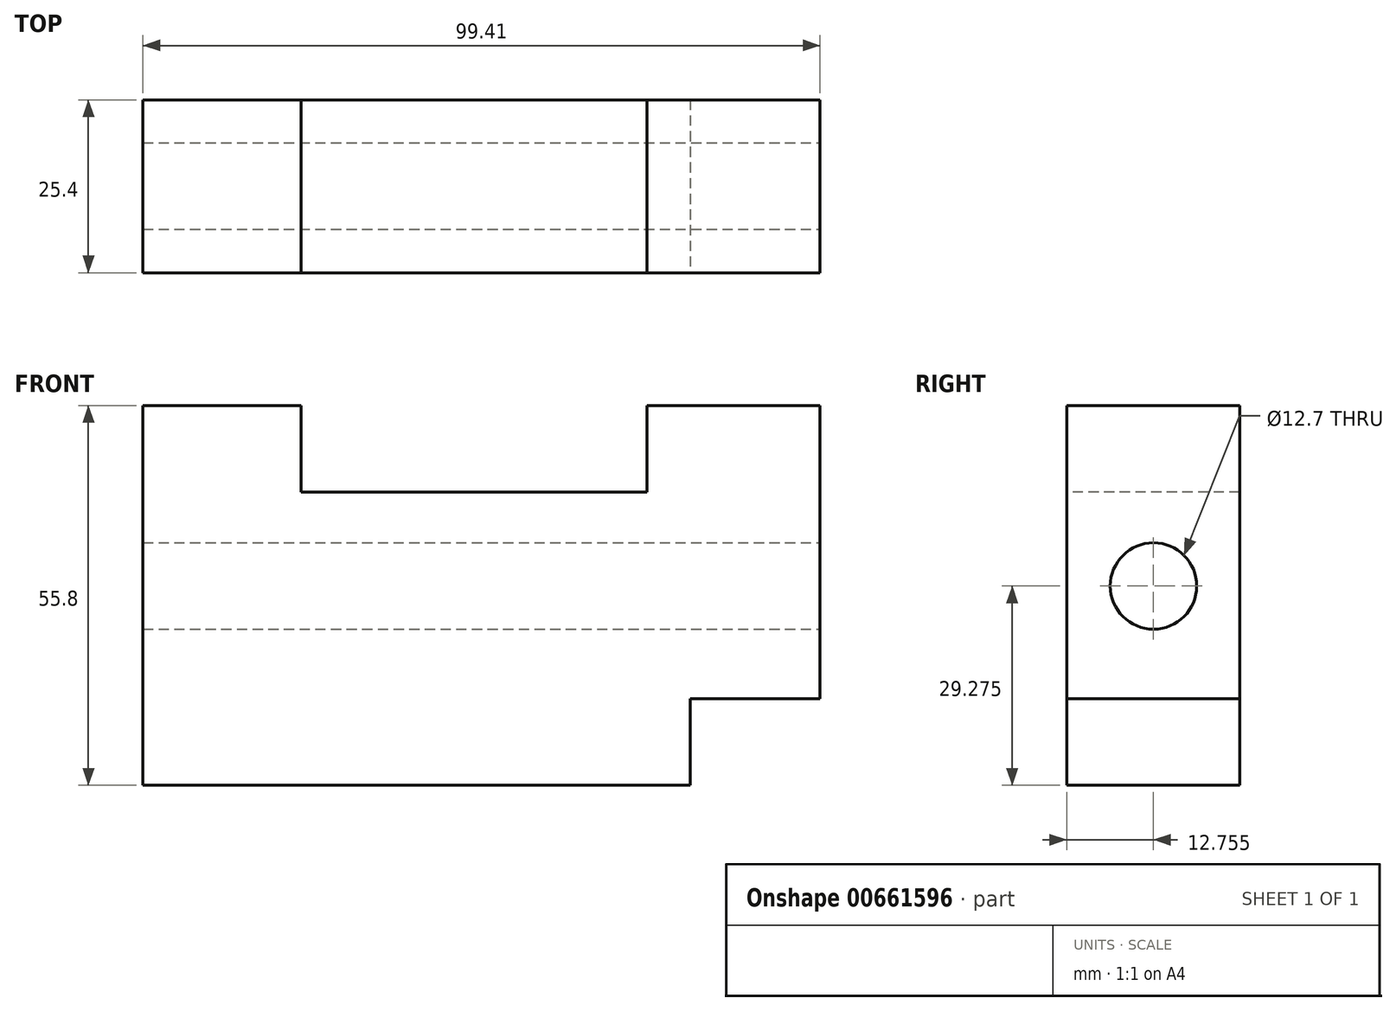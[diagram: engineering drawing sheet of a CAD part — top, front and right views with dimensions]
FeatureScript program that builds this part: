
annotation { "Feature Type Name" : "Feature", "Feature Type Description" : "" }
export const myFeature = defineFeature(function(context is Context, id is Id, definition is map)
    precondition{}
    {
        {
            var Q0;
            Q0=qCreatedBy(makeId("Front.planeOp"),FACE);
            var sketch = newSketch(context, id + "F0", { "sketchPlane" : qUnion([Q0])});
            skLineSegment(sketch, "E0.bottom", {"start": v(0, 0) * mm, "end": v(-99.41, 0) * mm});
            skLineSegment(sketch, "E0.top", {"start": v(0, 55.8) * mm, "end": v(-99.41, 55.8) * mm});
            skLineSegment(sketch, "E0.left", {"start": v(0, 0) * mm, "end": v(0, 55.8) * mm});
            skLineSegment(sketch, "E0.right", {"start": v(-99.41, 0) * mm, "end": v(-99.41, 55.8) * mm});
            skSolve(sketch);
        }
        {
            var Q0;
            Q0=makeQuery(id+"F0.imprint","IMPRINT",FACE,{"disambiguationData":[TD([[makeQuery(id+"F0.imprint","IMPRINT",EDGE,{"derivedFrom":sQuery(id+"F0.wireOp",EDGE,"E0.bottom")}),-1.0]])]});
            extrude(context, id + "F1", {"entities" : qUnion([Q0]), "depth" : 25.4 * mm, "offsetDistance" : 25.4 * mm});
        }
        {
            var Q0;
            Q0=makeQuery(id+"F1.opExtrude","CAP_FACE",FACE,{"disambiguationData":[OSD([sQuery(id+"F0.wireOp",EDGE,"E0.bottom"),sQuery(id+"F0.wireOp",EDGE,"E0.top"),sQuery(id+"F0.wireOp",EDGE,"E0.left"),sQuery(id+"F0.wireOp",EDGE,"E0.right")])],"isStart":false});
            var sketch = newSketch(context, id + "F2", { "sketchPlane" : qUnion([Q0])});
            skLineSegment(sketch, "E1.bottom", {"start": v(-76.2, 55.8) * mm, "end": v(-25.4, 55.8) * mm});
            skLineSegment(sketch, "E1.top", {"start": v(-76.2, 43.1) * mm, "end": v(-25.4, 43.1) * mm});
            skLineSegment(sketch, "E1.left", {"start": v(-76.2, 55.8) * mm, "end": v(-76.2, 43.1) * mm});
            skLineSegment(sketch, "E1.right", {"start": v(-25.4, 55.8) * mm, "end": v(-25.4, 43.1) * mm});
            skSolve(sketch);
        }
        {
            var Q0;
            Q0 = qSketchRegion(id + "F2", true);
            extrude(context, id + "F3", {"entities" : qUnion([Q0]), "operationType" : NewBodyOperationType.REMOVE, "oppositeDirection" : true, "depth" : 25.4 * mm, "offsetDistance" : 25.4 * mm});
        }
        {
            var Q0;
            Q0=makeQuery(id+"F1.opExtrude","CAP_FACE",FACE,{"disambiguationData":[OSD([sQuery(id+"F0.wireOp",EDGE,"E0.bottom"),sQuery(id+"F0.wireOp",EDGE,"E0.top"),sQuery(id+"F0.wireOp",EDGE,"E0.left"),sQuery(id+"F0.wireOp",EDGE,"E0.right")])],"isStart":false});
            var sketch = newSketch(context, id + "F4", { "sketchPlane" : qUnion([Q0])});
            skLineSegment(sketch, "E2.bottom", {"start": v(0, 0) * mm, "end": v(-19.05, 0) * mm});
            skLineSegment(sketch, "E2.top", {"start": v(0, 12.7) * mm, "end": v(-19.05, 12.7) * mm});
            skLineSegment(sketch, "E2.left", {"start": v(0, 0) * mm, "end": v(0, 12.7) * mm});
            skLineSegment(sketch, "E2.right", {"start": v(-19.05, 0) * mm, "end": v(-19.05, 12.7) * mm});
            skSolve(sketch);
        }
        {
            var Q0;
            Q0 = qSketchRegion(id + "F4", true);
            extrude(context, id + "F5", {"entities" : qUnion([Q0]), "operationType" : NewBodyOperationType.REMOVE, "oppositeDirection" : true, "depth" : 25.4 * mm, "offsetDistance" : 25.4 * mm});
        }
        {
            var Q0;
            Q0=makeQuery(id+"F1.opExtrude","SWEPT_FACE",FACE,{"disambiguationData":[OSD([sQuery(id+"F0.wireOp",EDGE,"E0.left")])]});
            var sketch = newSketch(context, id + "F6", { "sketchPlane" : qUnion([Q0])});
            skLineSegment(sketch, "E3", {"start": v(-25.4, 55.8) * mm, "end": v(-25.4, 43.1) * mm});
            skSolve(sketch);
        }
        {
            var Q0;
            {var subQ2=sQuery(id+"F6.wireOp",EDGE,"E3");Q0=makeQuery(id+"F6.imprint","IMPRINT",FACE,{"disambiguationData":[TD([[makeQuery(id+"F6.imprint","IMPRINT",EDGE,{"derivedFrom":subQ2}),-1.0]])]});}
            var sketch = newSketch(context, id + "F7", { "sketchPlane" : qUnion([Q0])});
            skCircle(sketch, "E4", {"center": v(-12.64, 29.27) * mm, "radius": 6.35 * mm});
            skSolve(sketch);
        }
        {
            var Q0;
            Q0 = qSketchRegion(id + "F7", true);
            extrude(context, id + "F8", {"entities" : qUnion([Q0]), "operationType" : NewBodyOperationType.REMOVE, "oppositeDirection" : true, "depth" : 101.6 * mm, "offsetDistance" : 25.4 * mm});
        }
    });
